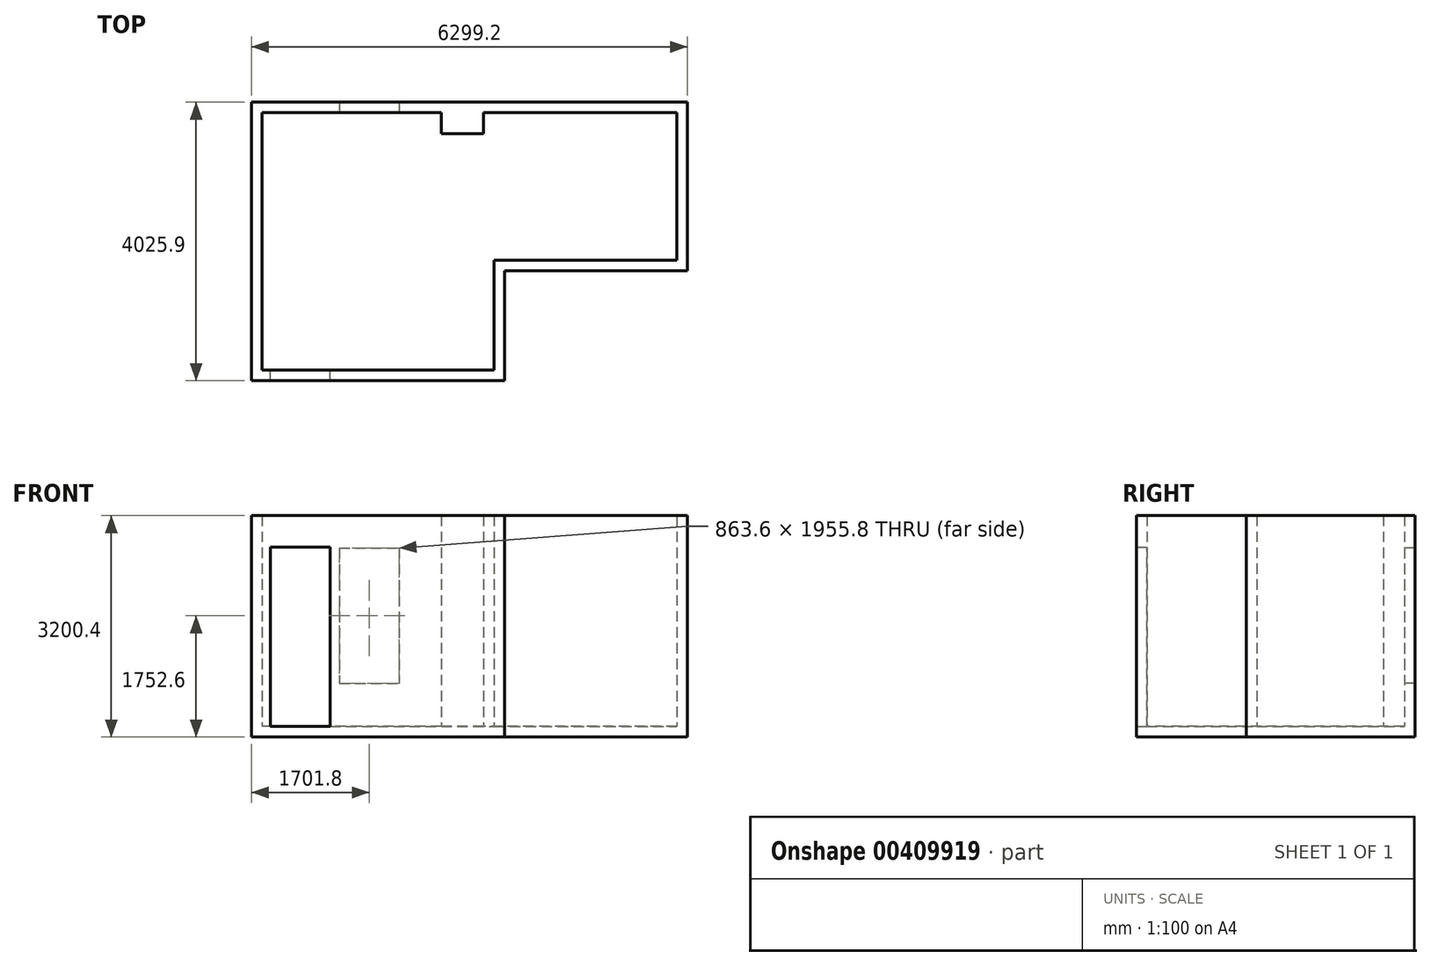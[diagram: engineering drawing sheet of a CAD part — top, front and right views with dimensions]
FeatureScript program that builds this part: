
annotation { "Feature Type Name" : "Feature", "Feature Type Description" : "" }
export const myFeature = defineFeature(function(context is Context, id is Id, definition is map)
    precondition{}
    {
        {
            var Q0;
            Q0=qCreatedBy(makeId("Top.planeOp"),FACE);
            var sketch = newSketch(context, id + "F0", { "sketchPlane" : qUnion([Q0])});
            skLineSegment(sketch, "E0", {"start": v(0, 0) * mm, "end": v(0, -3721.1) * mm});
            skLineSegment(sketch, "E1", {"start": v(0, -3721.1) * mm, "end": v(3352.8, -3721.1) * mm});
            skLineSegment(sketch, "E2", {"start": v(3352.8, -3721.1) * mm, "end": v(3352.8, -2133.6) * mm});
            skLineSegment(sketch, "E3", {"start": v(3352.8, -2133.6) * mm, "end": v(5994.4, -2133.6) * mm});
            skLineSegment(sketch, "E4", {"start": v(5994.4, -2133.6) * mm, "end": v(5994.4, 0) * mm});
            skLineSegment(sketch, "E5", {"start": v(5994.4, 0) * mm, "end": v(0, 0) * mm});
            skLineSegment(sketch, "E6.0", {"start": v(6146.8, 152.4) * mm, "end": v(-152.4, 152.4) * mm});
            skLineSegment(sketch, "E6.1", {"start": v(-152.4, -3873.5) * mm, "end": v(3505.2, -3873.5) * mm});
            skLineSegment(sketch, "E6.2", {"start": v(3505.2, -3873.5) * mm, "end": v(3505.2, -2286) * mm});
            skLineSegment(sketch, "E6.3", {"start": v(-152.4, 152.4) * mm, "end": v(-152.4, -3873.5) * mm});
            skLineSegment(sketch, "E6.4", {"start": v(3505.2, -2286) * mm, "end": v(6146.8, -2286) * mm});
            skLineSegment(sketch, "E6.5", {"start": v(6146.8, -2286) * mm, "end": v(6146.8, 152.4) * mm});
            skSolve(sketch);
        }
        {
            var Q0;
            Q0=makeQuery(id+"F0.imprint","IMPRINT",FACE,{"disambiguationData":[TD([[makeQuery(id+"F0.imprint","IMPRINT",EDGE,{"derivedFrom":sQuery(id+"F0.wireOp",EDGE,"E0")}),-1.0]])]});
            extrude(context, id + "F1", {"entities" : qUnion([Q0]), "depth" : 3048 * mm});
        }
        {
            var Q0;
            Q0=makeQuery(id+"F1.opExtrude","CAP_FACE",FACE,{"disambiguationData":[OSD([sQuery(id+"F0.wireOp",EDGE,"E0"),sQuery(id+"F0.wireOp",EDGE,"E1"),sQuery(id+"F0.wireOp",EDGE,"E2"),sQuery(id+"F0.wireOp",EDGE,"E3"),sQuery(id+"F0.wireOp",EDGE,"E4"),sQuery(id+"F0.wireOp",EDGE,"E5"),sQuery(id+"F0.wireOp",EDGE,"E6.0"),sQuery(id+"F0.wireOp",EDGE,"E6.1"),sQuery(id+"F0.wireOp",EDGE,"E6.2"),sQuery(id+"F0.wireOp",EDGE,"E6.3"),sQuery(id+"F0.wireOp",EDGE,"E6.4"),sQuery(id+"F0.wireOp",EDGE,"E6.5")])],"isStart":true});
            var sketch = newSketch(context, id + "F2", { "sketchPlane" : qUnion([Q0])});
            skLineSegment(sketch, "E7", {"start": v(-152.4, -152.4) * mm, "end": v(-152.4, 3873.5) * mm});
            skLineSegment(sketch, "E8", {"start": v(-152.4, 3873.5) * mm, "end": v(3505.2, 3873.5) * mm});
            skLineSegment(sketch, "E9", {"start": v(3505.2, 3873.5) * mm, "end": v(3505.2, 2286) * mm});
            skLineSegment(sketch, "E10", {"start": v(3505.2, 2286) * mm, "end": v(6146.8, 2286) * mm});
            skLineSegment(sketch, "E11", {"start": v(6146.8, 2286) * mm, "end": v(6146.8, -152.4) * mm});
            skLineSegment(sketch, "E12", {"start": v(6146.8, -152.4) * mm, "end": v(-152.4, -152.4) * mm});
            skSolve(sketch);
        }
        {
            var Q0;
            Q0 = qSketchRegion(id + "F2", true);
            extrude(context, id + "F3", {"entities" : qUnion([Q0]), "operationType" : NewBodyOperationType.ADD, "depth" : 152.4 * mm});
        }
        {
            var Q0;
            Q0=makeQuery(id+"F1.opExtrude","SWEPT_FACE",FACE,{"disambiguationData":[OSD([sQuery(id+"F0.wireOp",EDGE,"E1")])]});
            var sketch = newSketch(context, id + "F4", { "sketchPlane" : qUnion([Q0])});
            skLineSegment(sketch, "E13.bottom", {"start": v(-120.65, 0) * mm, "end": v(-984.25, 0) * mm});
            skLineSegment(sketch, "E13.top", {"start": v(-120.65, 2590.8) * mm, "end": v(-984.25, 2590.8) * mm});
            skLineSegment(sketch, "E13.left", {"start": v(-120.65, 0) * mm, "end": v(-120.65, 2590.8) * mm});
            skLineSegment(sketch, "E13.right", {"start": v(-984.25, 0) * mm, "end": v(-984.25, 2590.8) * mm});
            skSolve(sketch);
        }
        {
            var Q0;
            Q0 = qSketchRegion(id + "F4", true);
            extrude(context, id + "F5", {"entities" : qUnion([Q0]), "operationType" : NewBodyOperationType.REMOVE, "endBound" : BoundingType.THROUGH_ALL, "oppositeDirection" : true, "depth" : 25.4 * mm});
        }
        {
            var Q0;
            Q0=makeQuery(id+"F1.opExtrude","SWEPT_FACE",FACE,{"disambiguationData":[OSD([sQuery(id+"F0.wireOp",EDGE,"E5")])]});
            var sketch = newSketch(context, id + "F6", { "sketchPlane" : qUnion([Q0])});
            skLineSegment(sketch, "E14.bottom", {"start": v(1117.6, 2578.1) * mm, "end": v(1981.2, 2578.1) * mm});
            skLineSegment(sketch, "E14.top", {"start": v(1117.6, 622.3) * mm, "end": v(1981.2, 622.3) * mm});
            skLineSegment(sketch, "E14.left", {"start": v(1117.6, 2578.1) * mm, "end": v(1117.6, 622.3) * mm});
            skLineSegment(sketch, "E14.right", {"start": v(1981.2, 2578.1) * mm, "end": v(1981.2, 622.3) * mm});
            skSolve(sketch);
        }
        {
            var Q0;
            Q0 = qSketchRegion(id + "F6", true);
            extrude(context, id + "F7", {"entities" : qUnion([Q0]), "operationType" : NewBodyOperationType.REMOVE, "endBound" : BoundingType.THROUGH_ALL, "oppositeDirection" : true, "depth" : 25.4 * mm});
        }
        {
            var Q0;
            Q0=makeQuery(id+"F5.boolean.opBoolean","MERGE",FACE,{"derivedFrom":[makeQuery(id+"F3.opExtrude","CAP_FACE",FACE,{"disambiguationData":[OSD([sQuery(id+"F2.wireOp",EDGE,"E7"),sQuery(id+"F2.wireOp",EDGE,"E8"),sQuery(id+"F2.wireOp",EDGE,"E9"),sQuery(id+"F2.wireOp",EDGE,"E10"),sQuery(id+"F2.wireOp",EDGE,"E11"),sQuery(id+"F2.wireOp",EDGE,"E12")])],"isStart":true}),makeQuery(id+"F5.opExtrude","SWEPT_FACE",FACE,{"disambiguationData":[OSD([sQuery(id+"F4.wireOp",EDGE,"E13.bottom")])]})]});
            var sketch = newSketch(context, id + "F8", { "sketchPlane" : qUnion([Q0])});
            skLineSegment(sketch, "E15.bottom", {"start": v(3200.4, 0) * mm, "end": v(2590.8, 0) * mm});
            skLineSegment(sketch, "E15.top", {"start": v(3200.4, -304.8) * mm, "end": v(2590.8, -304.8) * mm});
            skLineSegment(sketch, "E15.left", {"start": v(3200.4, 0) * mm, "end": v(3200.4, -304.8) * mm});
            skLineSegment(sketch, "E15.right", {"start": v(2590.8, 0) * mm, "end": v(2590.8, -304.8) * mm});
            skSolve(sketch);
        }
        {
            var Q0;
            Q0 = qSketchRegion(id + "F8", true);
            var Q1;
            Q1=makeQuery(id+"F1.opExtrude","CAP_FACE",FACE,{"disambiguationData":[OSD([sQuery(id+"F0.wireOp",EDGE,"E0"),sQuery(id+"F0.wireOp",EDGE,"E1"),sQuery(id+"F0.wireOp",EDGE,"E2"),sQuery(id+"F0.wireOp",EDGE,"E3"),sQuery(id+"F0.wireOp",EDGE,"E4"),sQuery(id+"F0.wireOp",EDGE,"E5"),sQuery(id+"F0.wireOp",EDGE,"E6.0"),sQuery(id+"F0.wireOp",EDGE,"E6.1"),sQuery(id+"F0.wireOp",EDGE,"E6.2"),sQuery(id+"F0.wireOp",EDGE,"E6.3"),sQuery(id+"F0.wireOp",EDGE,"E6.4"),sQuery(id+"F0.wireOp",EDGE,"E6.5")])],"isStart":false});
            extrude(context, id + "F9", {"entities" : qUnion([Q0]), "operationType" : NewBodyOperationType.ADD, "endBound" : BoundingType.UP_TO_SURFACE, "endBoundEntityFace" : qUnion([Q1]), "depth" : 25.4 * mm});
        }
    });
